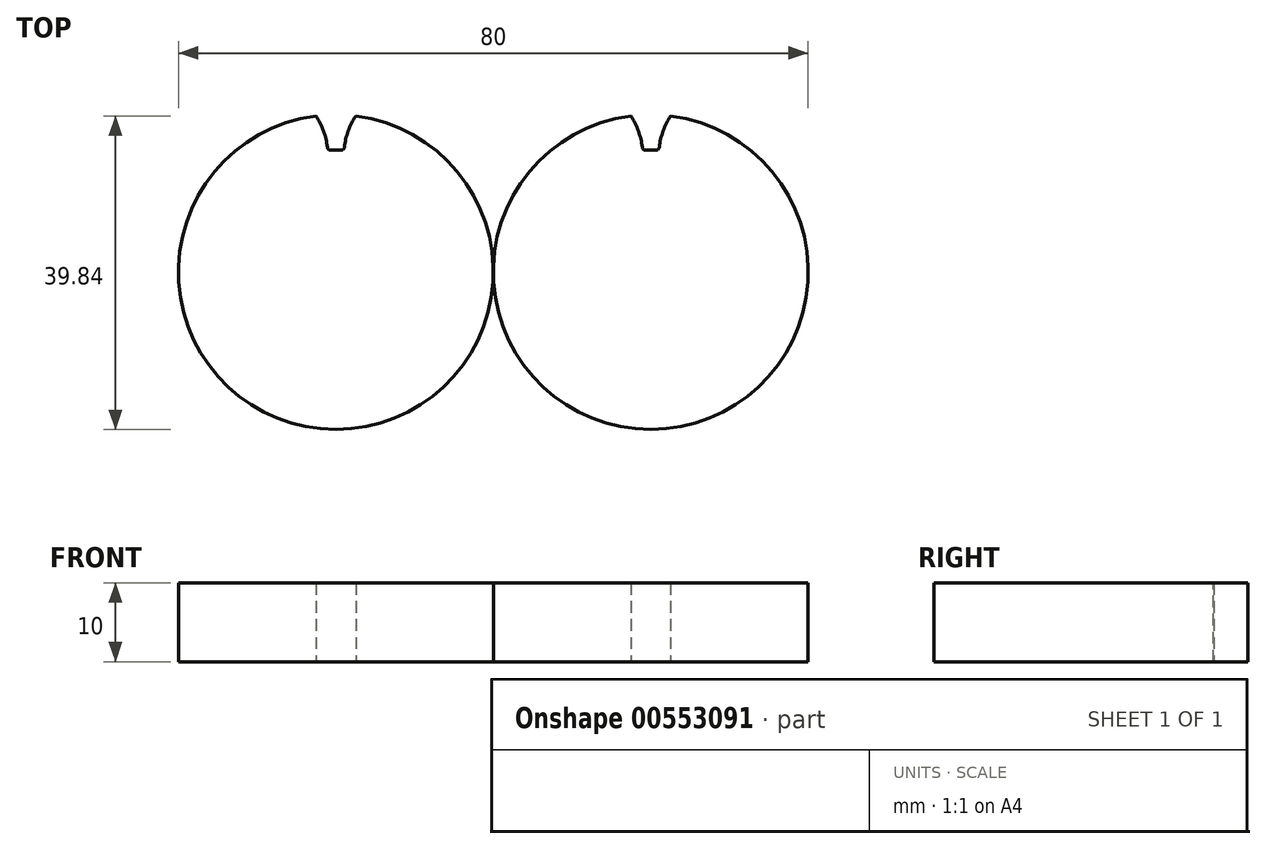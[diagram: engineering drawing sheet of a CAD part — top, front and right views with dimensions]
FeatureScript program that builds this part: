
annotation { "Feature Type Name" : "Feature", "Feature Type Description" : "" }
export const myFeature = defineFeature(function(context is Context, id is Id, definition is map)
    precondition{}
    {
        {
            var Q0;
            Q0=qCreatedBy(makeId("Top.planeOp"),FACE);
            var sketch = newSketch(context, id + "F0", { "sketchPlane" : qUnion([Q0])});
            skCircle(sketch, "E0", {"center": v(0, 0) * mm, "radius": 18 * mm, "construction": true});
            skCircle(sketch, "E1", {"center": v(0, 0) * mm, "radius": 20 * mm});
            skCircle(sketch, "E2", {"center": v(0, 0) * mm, "radius": 15.5 * mm});
            skArc(sketch, "E3", {"start": v(-1.05, 15.46) * mm, "mid": v(-1.5, 17.75) * mm, "end": v(-2.53, 19.84) * mm});
            skArc(sketch, "E4.MirrorCS", {"start": v(1.05, 15.46) * mm, "mid": v(1.5, 17.75) * mm, "end": v(2.53, 19.84) * mm});
            skLineSegment(sketch, "E5", {"start": v(-1.05, 15.46) * mm, "end": v(0, 0) * mm, "construction": true});
            skLineSegment(sketch, "E6", {"start": v(-1.57, 17.93) * mm, "end": v(1.57, 17.93) * mm, "construction": true});
            skLineSegment(sketch, "E7", {"start": v(0, 13.62) * mm, "end": v(-1.57, 17.93) * mm, "construction": true});
            skLineSegment(sketch, "E8", {"start": v(1.57, 17.93) * mm, "end": v(4.66, 17.39) * mm, "construction": true});
            skLineSegment(sketch, "E9", {"start": v(0, 0) * mm, "end": v(3.47, 19.7) * mm, "construction": true});
            skSolve(sketch);
        }
        {
            var Q0;
            {var subQ0=sQuery(id+"F0.wireOp",EDGE,"E3");Q0=makeQuery(id+"F0.imprint","IMPRINT",FACE,{"disambiguationData":[TD([[makeQuery(id+"F0.imprint","IMPRINT",EDGE,{"derivedFrom":subQ0}),1.0]])]});}
            var Q1;
            {var subQ0=sQuery(id+"F0.wireOp",EDGE,"E2");var subQ1=makeQuery(id+"F0.imprint","INTERSECT",VERTEX,{"derivedFrom":[subQ0,sQuery(id+"F0.wireOp",EDGE,"E3")]});Q1=makeQuery(id+"F0.imprint","IMPRINT",FACE,{"disambiguationData":[TD([[makeQuery(id+"F0.imprint","IMPRINT",EDGE,{"disambiguationData":[TD([[subQ1,1.0]])],"derivedFrom":subQ0}),1.0]])]});}
            var Q2;
            {var subQ0=sQuery(id+"F0.wireOp",EDGE,"E3");Q2=makeQuery(id+"F0.imprint","IMPRINT",FACE,{"disambiguationData":[TD([[makeQuery(id+"F0.imprint","IMPRINT",EDGE,{"derivedFrom":subQ0}),-1.0]])]});}
            var Q3;
            Q3=sQuery(id+"F0.wireOp",EDGE,"E1");
            extrude(context, id + "F1", {"entities" : qUnion([Q0, Q1, Q2]), "surfaceEntities" : qUnion([Q3]), "depth" : 10 * mm, "offsetDistance" : 25 * mm});
        }
        {
            var Q0;
            {var subQ0=sQuery(id+"F0.wireOp",EDGE,"E3");Q0=makeQuery(id+"F0.imprint","IMPRINT",FACE,{"disambiguationData":[TD([[makeQuery(id+"F0.imprint","IMPRINT",EDGE,{"derivedFrom":subQ0}),-1.0]])]});}
            extrude(context, id + "F2", {"entities" : qUnion([Q0]), "operationType" : NewBodyOperationType.REMOVE, "depth" : 10 * mm, "offsetDistance" : 25 * mm});
        }
        {
            var Q0;
            Q0=makeQuery(id+"F2.boolean.opBoolean","COPY",EDGE,{"derivedFrom":makeQuery(id+"F2.opExtrude","SWEPT_EDGE",EDGE,{"disambiguationData":[OSD([sQuery(id+"F0.wireOp",EDGE,"E2"),sQuery(id+"F0.wireOp",EDGE,"E3")])]})});
            var Q1;
            Q1=makeQuery(id+"F2.boolean.opBoolean","COPY",EDGE,{"derivedFrom":makeQuery(id+"F2.opExtrude","SWEPT_EDGE",EDGE,{"disambiguationData":[OSD([sQuery(id+"F0.wireOp",EDGE,"E1"),sQuery(id+"F0.wireOp",EDGE,"E4.MirrorCS")])]})});
            var Q2;
            Q2=makeQuery(id+"F2.boolean.opBoolean","COPY",EDGE,{"derivedFrom":makeQuery(id+"F2.opExtrude","SWEPT_EDGE",EDGE,{"disambiguationData":[OSD([sQuery(id+"F0.wireOp",EDGE,"E2"),sQuery(id+"F0.wireOp",EDGE,"E4.MirrorCS")])]})});
            var Q3;
            Q3=makeQuery(id+"F2.boolean.opBoolean","COPY",EDGE,{"derivedFrom":makeQuery(id+"F2.opExtrude","SWEPT_EDGE",EDGE,{"disambiguationData":[OSD([sQuery(id+"F0.wireOp",EDGE,"E1"),sQuery(id+"F0.wireOp",EDGE,"E3")])]})});
            fillet(context, id + "F3", {"entities" : qUnion([Q0, Q1, Q2, Q3]), "radius" : .4 * mm, "tangentPropagation" : true, "allowEdgeOverflow" : false});
        }
        {
            var Q0;
            Q0=makeQuery(id+"F1.opExtrude","SWEPT_BODY",BODY,{"disambiguationData":[OSD([sQuery(id+"F0.wireOp",EDGE,"E1")])]});
            transform(context, id + "F4", {"entities" : qUnion([Q0]), "transformType" : TransformType.TRANSLATION_3D, "dx" : 40 * mm, "dy" : 0 * mm, "dz" : 0 * mm, "makeCopy" : true});
        }
    });
